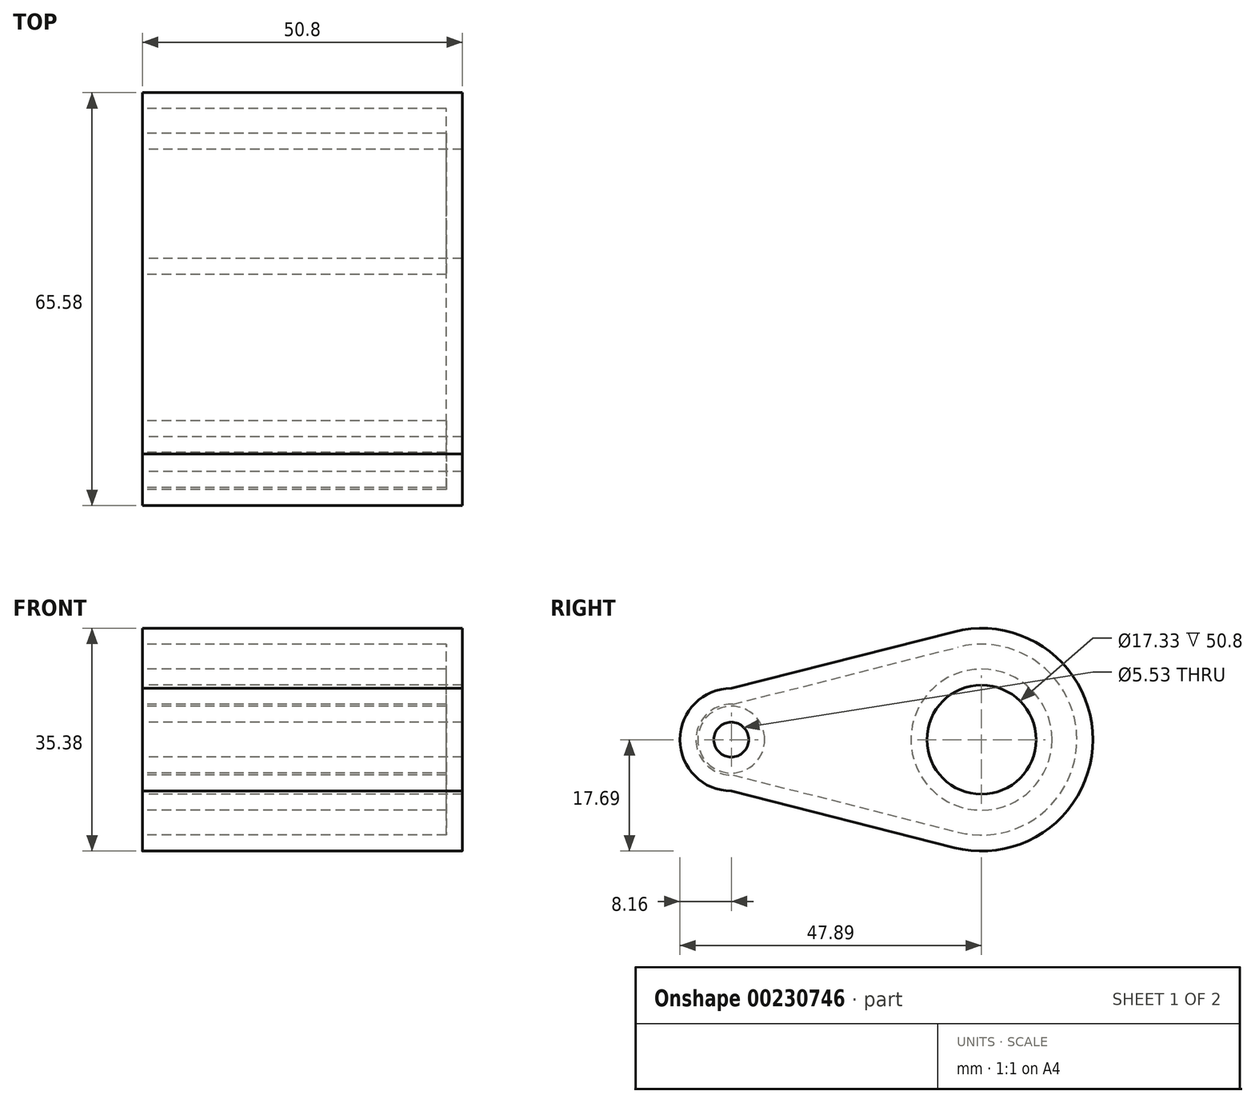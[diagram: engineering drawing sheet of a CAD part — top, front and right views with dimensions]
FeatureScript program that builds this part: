
annotation { "Feature Type Name" : "Feature", "Feature Type Description" : "" }
export const myFeature = defineFeature(function(context is Context, id is Id, definition is map)
    precondition{}
    {
        {
            var Q0;
            Q0=qCreatedBy(makeId("Right.planeOp"),FACE);
            var sketch = newSketch(context, id + "F0", { "sketchPlane" : qUnion([Q0])});
            skCircle(sketch, "E0", {"center": v(0, 0) * mm, "radius": 8.16 * mm});
            skCircle(sketch, "E1", {"center": v(39.73, 0) * mm, "radius": 17.7 * mm});
            skLineSegment(sketch, "E2", {"start": v(0, 8.16) * mm, "end": v(35.37, 17.15) * mm});
            skLineSegment(sketch, "E3", {"start": v(0, -8.16) * mm, "end": v(35.37, -17.15) * mm});
            skSolve(sketch);
        }
        {
            var Q0;
            {var subQ0=sQuery(id+"F0.wireOp",EDGE,"E0");var subQ1=makeQuery(id+"F0.imprint","INTERSECT",VERTEX,{"derivedFrom":[subQ0,sQuery(id+"F0.wireOp",EDGE,"E2")]});Q0=makeQuery(id+"F0.imprint","IMPRINT",FACE,{"disambiguationData":[TD([[makeQuery(id+"F0.imprint","IMPRINT",EDGE,{"disambiguationData":[TD([[subQ1,-1.0]])],"derivedFrom":subQ0}),1.0]])]});}
            var Q1;
            {var subQ0=sQuery(id+"F0.wireOp",EDGE,"E1");var subQ1=makeQuery(id+"F0.imprint","INTERSECT",VERTEX,{"derivedFrom":[subQ0,sQuery(id+"F0.wireOp",EDGE,"E2")]});Q1=makeQuery(id+"F0.imprint","IMPRINT",FACE,{"disambiguationData":[TD([[makeQuery(id+"F0.imprint","IMPRINT",EDGE,{"disambiguationData":[TD([[subQ1,-1.0]])],"derivedFrom":subQ0}),1.0]])]});}
            var Q2;
            {var subQ0=sQuery(id+"F0.wireOp",EDGE,"E2");Q2=makeQuery(id+"F0.imprint","IMPRINT",FACE,{"disambiguationData":[TD([[makeQuery(id+"F0.imprint","IMPRINT",EDGE,{"derivedFrom":subQ0}),-1.0]])]});}
            extrude(context, id + "F1", {"entities" : qUnion([Q0, Q1, Q2]), "depth" : 50.8 * mm});
        }
        {
            var Q0;
            Q0=makeQuery(id+"F1.opExtrude","CAP_FACE",FACE,{"disambiguationData":[OSD([sQuery(id+"F0.wireOp",EDGE,"E0"),sQuery(id+"F0.wireOp",EDGE,"E1"),sQuery(id+"F0.wireOp",EDGE,"E2"),sQuery(id+"F0.wireOp",EDGE,"E3")])],"isStart":true});
            var sketch = newSketch(context, id + "F2", { "sketchPlane" : qUnion([Q0])});
            skCircle(sketch, "E4", {"center": v(0, 0) * mm, "radius": 2.76 * mm});
            skCircle(sketch, "E5", {"center": v(-39.73, 0) * mm, "radius": 8.67 * mm});
            skSolve(sketch);
        }
        {
            var Q0;
            Q0=makeQuery(id+"F2.imprint","IMPRINT",FACE,{"disambiguationData":[TD([[makeQuery(id+"F2.imprint","IMPRINT",EDGE,{"derivedFrom":sQuery(id+"F2.wireOp",EDGE,"E4")}),1.0]])]});
            var Q1;
            Q1=makeQuery(id+"F2.imprint","IMPRINT",FACE,{"disambiguationData":[TD([[makeQuery(id+"F2.imprint","IMPRINT",EDGE,{"derivedFrom":sQuery(id+"F2.wireOp",EDGE,"E5")}),1.0]])]});
            extrude(context, id + "F3", {"entities" : qUnion([Q0, Q1]), "operationType" : NewBodyOperationType.REMOVE, "oppositeDirection" : true, "depth" : 79.5 * mm});
        }
        {
            var Q0;
            Q0=makeQuery(id+"F1.opExtrude","CAP_FACE",FACE,{"disambiguationData":[OSD([sQuery(id+"F0.wireOp",EDGE,"E0"),sQuery(id+"F0.wireOp",EDGE,"E1"),sQuery(id+"F0.wireOp",EDGE,"E2"),sQuery(id+"F0.wireOp",EDGE,"E3")])],"isStart":true});
            shell(context, id + "F4", {"entities" : qUnion([Q0]), "thickness" : 2.54 * mm});
        }
    });
